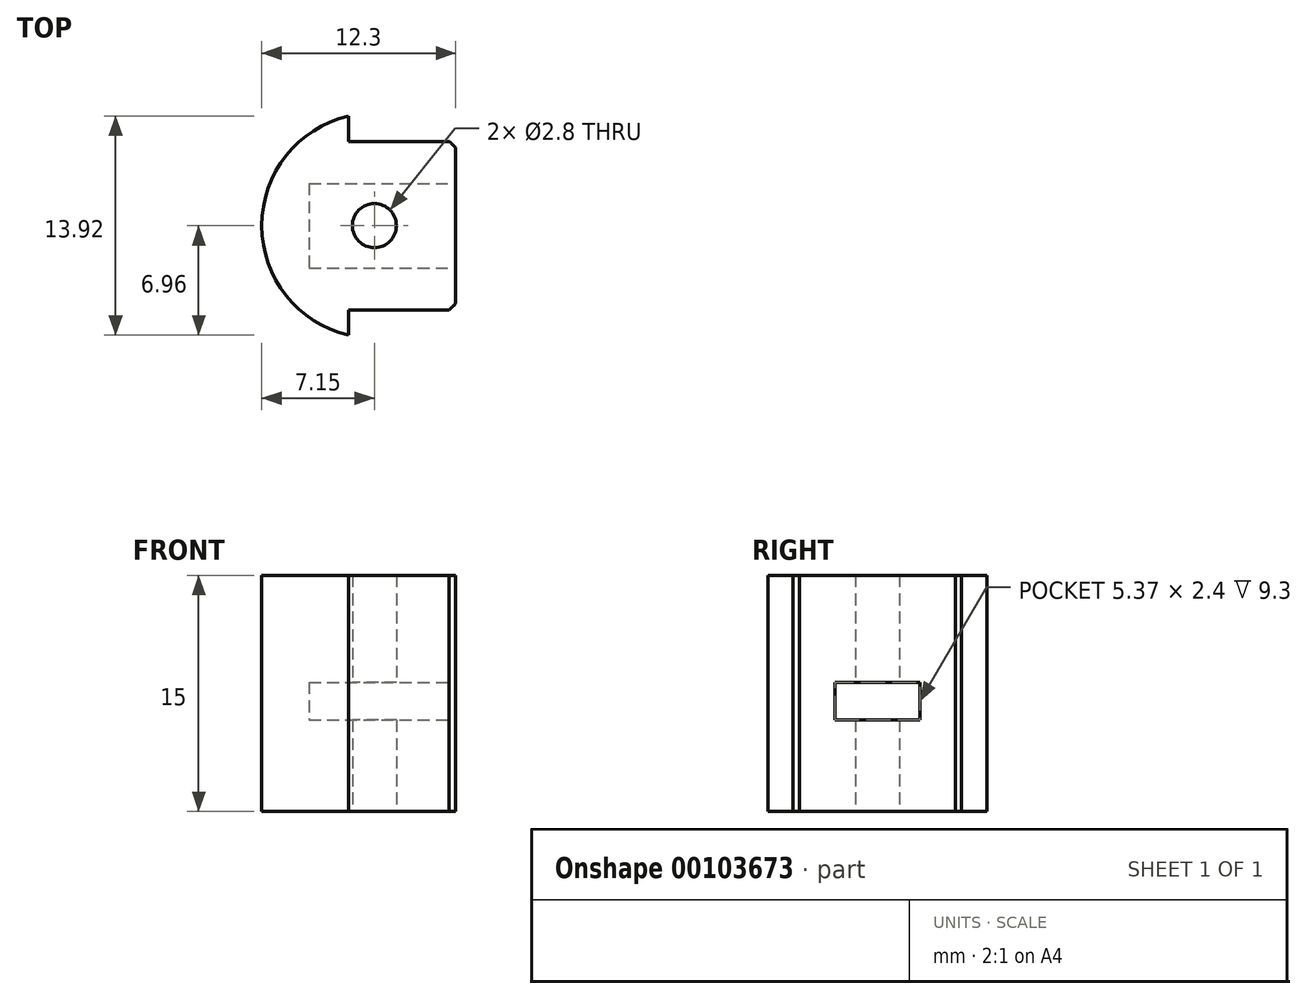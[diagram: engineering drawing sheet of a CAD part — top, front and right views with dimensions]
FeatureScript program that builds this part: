
annotation { "Feature Type Name" : "Feature", "Feature Type Description" : "" }
export const myFeature = defineFeature(function(context is Context, id is Id, definition is map)
    precondition{}
    {
        {
            var Q0;
            Q0=qCreatedBy(makeId("Top.planeOp"),FACE);
            var sketch = newSketch(context, id + "F0", { "sketchPlane" : qUnion([Q0])});
            skCircle(sketch, "E0", {"center": v(0, 0) * mm, "radius": 7.15 * mm});
            skLineSegment(sketch, "E1", {"start": v(-1.65, 6.96) * mm, "end": v(-1.65, -6.96) * mm});
            skLineSegment(sketch, "E2", {"start": v(-7.15, 0) * mm, "end": v(7.15, 0) * mm, "construction": true});
            skLineSegment(sketch, "E3", {"start": v(5.15, 4.96) * mm, "end": v(5.15, -4.96) * mm});
            skLineSegment(sketch, "E4", {"start": v(-1.65, 5.35) * mm, "end": v(5.15, 5.35) * mm});
            skLineSegment(sketch, "E5.MirrorCS", {"start": v(-1.65, -5.35) * mm, "end": v(5.15, -5.35) * mm});
            skCircle(sketch, "E6", {"center": v(0, 0) * mm, "radius": 1.4 * mm});
            skSolve(sketch);
        }
        {
            var Q0;
            {var subQ0=sQuery(id+"F0.wireOp",EDGE,"E1");var subQ1=sQuery(id+"F0.wireOp",EDGE,"E0");var subQ2=makeQuery(id+"F0.imprint","INTERSECT",VERTEX,{"disambiguationData":[OD(0.0)],"derivedFrom":[subQ1,subQ0]});Q0=makeQuery(id+"F0.imprint","IMPRINT",FACE,{"disambiguationData":[TD([[makeQuery(id+"F0.imprint","IMPRINT",EDGE,{"disambiguationData":[TD([[subQ2,-1.0]])],"derivedFrom":subQ1}),1.0]])]});}
            var Q1;
            {var subQ0=sQuery(id+"F0.wireOp",EDGE,"E4");Q1=makeQuery(id+"F0.imprint","IMPRINT",FACE,{"disambiguationData":[TD([[makeQuery(id+"F0.imprint","IMPRINT",EDGE,{"derivedFrom":subQ0}),-1.0]])]});}
            extrude(context, id + "F1", {"entities" : qUnion([Q0, Q1]), "depth" : 15 * mm});
        }
        {
            var Q0;
            Q0=makeQuery(id+"F1.opExtrude","SWEPT_FACE",FACE,{"disambiguationData":[OSD([sQuery(id+"F0.wireOp",EDGE,"E3")])]});
            var sketch = newSketch(context, id + "F2", { "sketchPlane" : qUnion([Q0])});
            skLineSegment(sketch, "E7", {"start": v(0, 0) * mm, "end": v(0, 15) * mm, "construction": true});
            skPoint(sketch, "E8", {"position": v(0, 7) * mm});
            skLineSegment(sketch, "E9.bottom", {"start": v(2.69, 8.2) * mm, "end": v(-2.69, 8.2) * mm});
            skLineSegment(sketch, "E9.top", {"start": v(2.69, 5.8) * mm, "end": v(-2.69, 5.8) * mm});
            skLineSegment(sketch, "E9.left", {"start": v(2.69, 8.2) * mm, "end": v(2.69, 5.8) * mm});
            skLineSegment(sketch, "E9.right", {"start": v(-2.69, 8.2) * mm, "end": v(-2.69, 5.8) * mm});
            skSolve(sketch);
        }
        {
            var Q0;
            Q0=makeQuery(id+"F2.imprint","IMPRINT",FACE,{"disambiguationData":[TD([[makeQuery(id+"F2.imprint","IMPRINT",EDGE,{"derivedFrom":sQuery(id+"F2.wireOp",EDGE,"E9.bottom")}),1.0]])]});
            extrude(context, id + "F3", {"entities" : qUnion([Q0]), "operationType" : NewBodyOperationType.REMOVE, "oppositeDirection" : true, "depth" : 9.3 * mm});
        }
    });
